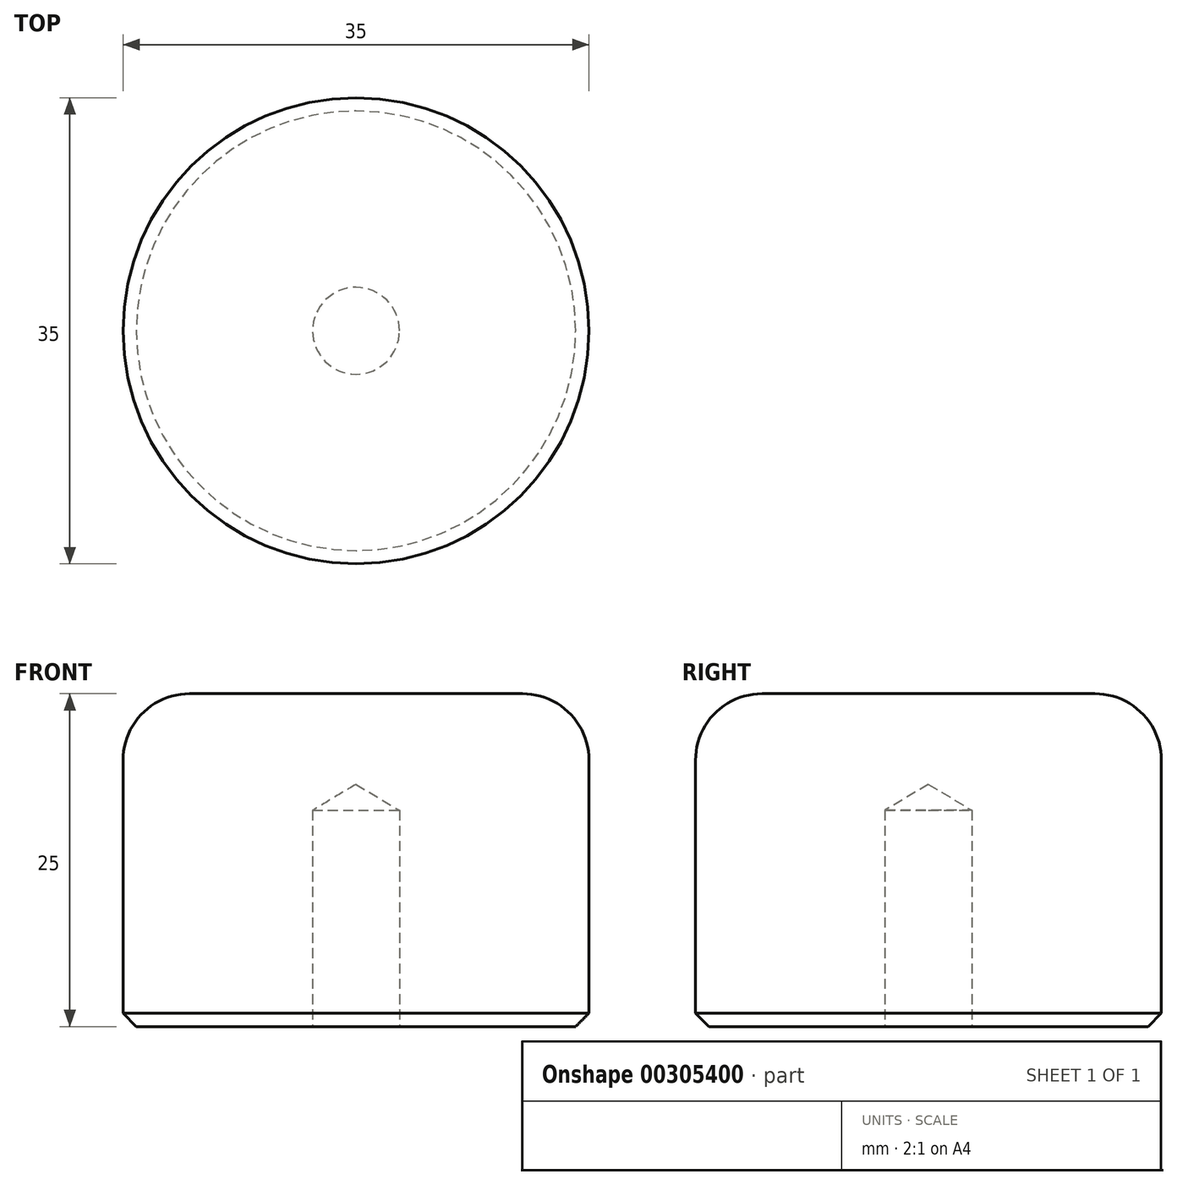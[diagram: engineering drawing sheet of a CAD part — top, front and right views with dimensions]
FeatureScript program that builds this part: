
annotation { "Feature Type Name" : "Feature", "Feature Type Description" : "" }
export const myFeature = defineFeature(function(context is Context, id is Id, definition is map)
    precondition{}
    {
        {
            var Q0;
            Q0=qCreatedBy(makeId("Top.planeOp"),FACE);
            var sketch = newSketch(context, id + "F0", { "sketchPlane" : qUnion([Q0])});
            skCircle(sketch, "E0", {"center": v(0, 0) * mm, "radius": 17.5 * mm});
            skSolve(sketch);
        }
        {
            var Q0;
            Q0 = qSketchRegion(id + "F0", true);
            extrude(context, id + "F1", {"entities" : qUnion([Q0]), "depth" : 25 * mm});
        }
        {
            var Q0;
            Q0=makeQuery(id+"F1.opExtrude","CAP_EDGE",EDGE,{"disambiguationData":[OSD([sQuery(id+"F0.wireOp",EDGE,"E0")])],"isStart":false});
            fillet(context, id + "F2", {"entities" : qUnion([Q0]), "radius" : 5 * mm, "tangentPropagation" : true, "allowEdgeOverflow" : false});
        }
        {
            var Q0;
            Q0=makeQuery(id+"F1.opExtrude","CAP_EDGE",EDGE,{"disambiguationData":[OSD([sQuery(id+"F0.wireOp",EDGE,"E0")])],"isStart":true});
            chamfer(context, id + "F3", {"entities" : qUnion([Q0]), "width" : 1 * mm, "tangentPropagation" : true});
        }
        {
            var Q0;
            Q0=sQuery(id+"F0.wireOp",VERTEX,"E0.center");
            var Q1;
            Q1=makeQuery(id+"F1.opExtrude","SWEPT_BODY",BODY,{"disambiguationData":[OSD([sQuery(id+"F0.wireOp",EDGE,"E0")])]});
            hole(context, id + "F4", {"style" : HoleStyle.SIMPLE, "endStyle" : HoleEndStyle.BLIND, "oppositeDirection" : true, "standardTappedOrClearance" : lookupTablePath({ "standard" : "ANSI", "engagement" : "75%", "pitch" : "18 tpi", "size" : "5/16", "type" : "Tapped" }), "standardBlindInLast" : lookupTablePath({ "standard" : "ANSI", "engagement" : "75%", "pitch" : "18 tpi", "size" : "5/16", "type" : "Tapped" }), "holeDiameter" : 6.53 * mm, "showTappedDepth" : true, "holeDepth" : 16.23 * mm, "tappedDepth" : 12 * mm, "tapClearance" : 3, "startFromSketch" : true, "locations" : qUnion([Q0]), "scope" : qUnion([Q1]), "majorDiameter" : 7.94 * mm});
        }
    });
